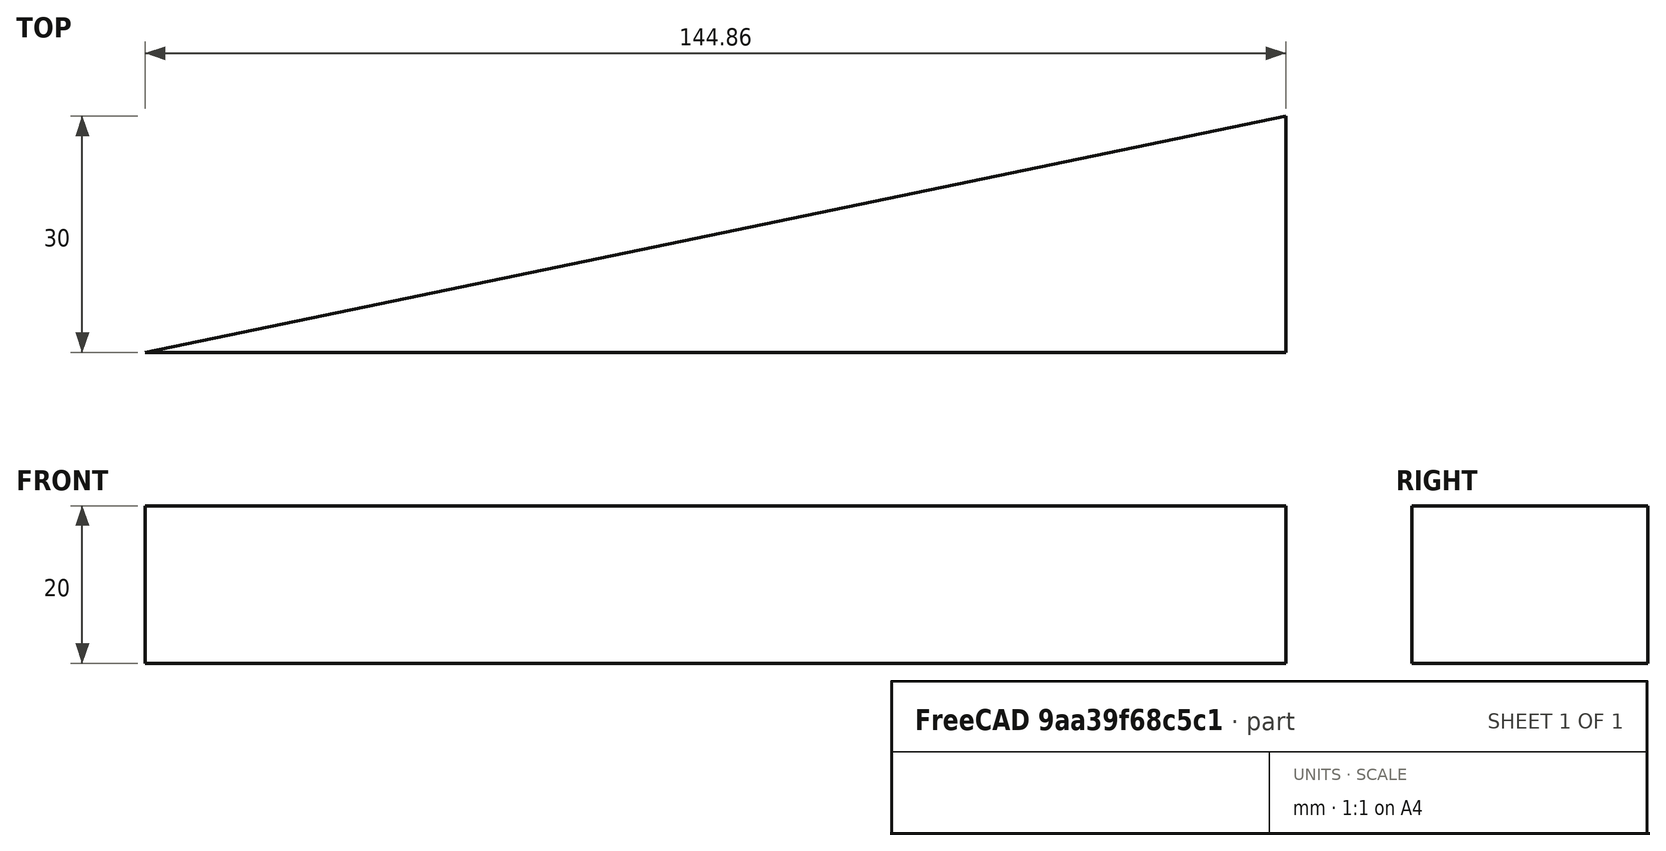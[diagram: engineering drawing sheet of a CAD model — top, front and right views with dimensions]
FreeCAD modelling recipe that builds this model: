
FCSTD DOCUMENT  (FreeCAD 0.21R33668 +26 (Git))
Label: TestWedge
License: All rights reserved
LicenseURL: http://en.wikipedia.org/wiki/All_rights_reserved
objects: Sketcher::SketchObject×1, PartDesign::Pad×1, PartDesign::Body×1
note: 4 computed .brp shape members not serialized (recipe doc carries the construction recipe); baked Part::Feature solids carry a one-line shape summary decoded from their .brp

FEATURE [Sketcher::SketchObject] Sketch
  FullyConstrained = true
  sketch-geometry (3):
    g0: LineSegment StartX=0 StartY=0 StartZ=0 EndX=144.865 EndY=0 EndZ=0
    g1: LineSegment StartX=144.865 StartY=0 StartZ=0 EndX=144.865 EndY=30 EndZ=0
    g2: LineSegment StartX=144.865 StartY=30 StartZ=0 EndX=0 EndY=0 EndZ=0
  constraints (8):
    c: Coincident(g-1,g0)
    c: PointOnObject(g0,g-1)
    c: Coincident(g0,g1)
    c: Vertical(g1)
    c: Coincident(g1,g2)
    c: Coincident(g2,g0)
    c: Angle(g0,g2) = 0.204204
    c: DistanceY(g1,g1) = 30
FEATURE [PartDesign::Pad] Pad
  Direction = (0,0,1)
  Length = 20
  Length2 = 10
  Profile = -> Sketch
  ReferenceAxis = -> Sketch [N_Axis]
  Type = 0
FEATURE [PartDesign::Body] Body  label="TestWedgeBody"
  Group = -> [Sketch,Pad]
  Origin = -> Origin
  Tip = -> Pad
